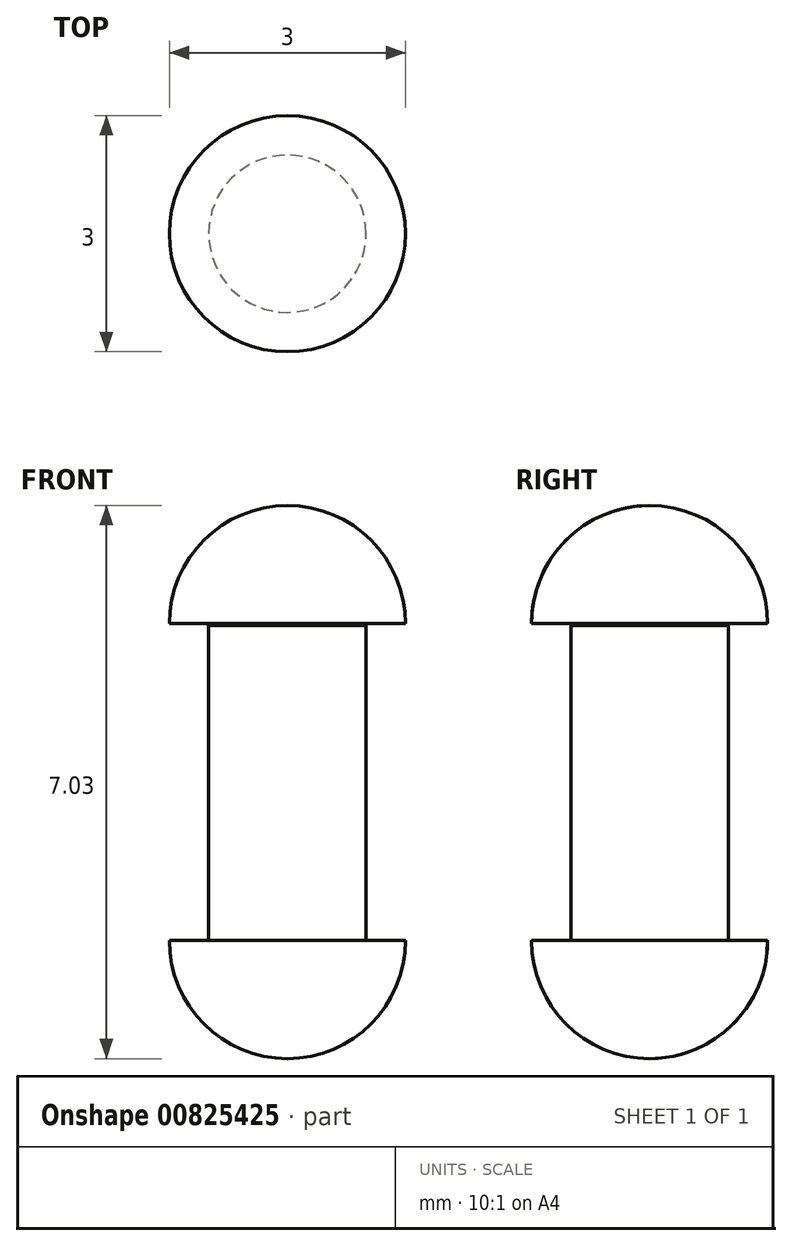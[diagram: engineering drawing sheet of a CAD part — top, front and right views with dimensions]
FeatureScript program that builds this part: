
annotation { "Feature Type Name" : "Feature", "Feature Type Description" : "" }
export const myFeature = defineFeature(function(context is Context, id is Id, definition is map)
    precondition{}
    {
        {
            var Q0;
            Q0=qCreatedBy(makeId("Top.planeOp"),FACE);
            var sketch = newSketch(context, id + "F0", { "sketchPlane" : qUnion([Q0])});
            skCircle(sketch, "E0", {"center": v(0, 0) * mm, "radius": 1 * mm});
            skSolve(sketch);
        }
        {
            var Q0;
            Q0=makeQuery(id+"F0.imprint","IMPRINT",FACE,{"disambiguationData":[TD([[makeQuery(id+"F0.imprint","IMPRINT",EDGE,{"derivedFrom":sQuery(id+"F0.wireOp",EDGE,"E0")}),1.0]])]});
            var Q1;
            Q1=sQuery(id+"F0.wireOp",EDGE,"E0");
            extrude(context, id + "F1", {"entities" : qUnion([Q0]), "surfaceEntities" : qUnion([Q1]), "depth" : 4 * mm, "offsetDistance" : 25 * mm});
        }
        {
            var Q0;
            Q0=qCreatedBy(makeId("Right.planeOp"),FACE);
            var sketch = newSketch(context, id + "F2", { "sketchPlane" : qUnion([Q0])});
            skArc(sketch, "E1", {"start": v(0, -1.5) * mm, "mid": v(1.06, -1.06) * mm, "end": v(1.5, 0) * mm});
            skLineSegment(sketch, "E2", {"start": v(0, 0) * mm, "end": v(1.5, 0) * mm});
            skLineSegment(sketch, "E3", {"start": v(0, 0) * mm, "end": v(0, -1.5) * mm});
            skSolve(sketch);
        }
        {
            var Q0;
            Q0=makeQuery(id+"F2.imprint","IMPRINT",FACE,{"disambiguationData":[TD([[makeQuery(id+"F2.imprint","IMPRINT",EDGE,{"derivedFrom":sQuery(id+"F2.wireOp",EDGE,"E1")}),1.0]])]});
            var Q1;
            Q1=sQuery(id+"F2.wireOp",EDGE,"E3");
            revolve(context, id + "F3", {"operationType" : NewBodyOperationType.ADD, "surfaceOperationType" : NewSurfaceOperationType.NEW, "entities" : qUnion([Q0]), "axis" : qUnion([Q1]), "revolveType" : RevolveType.FULL});
        }
        {
            var Q0;
            Q0=qCreatedBy(makeId("Right.planeOp"),FACE);
            var sketch = newSketch(context, id + "F4", { "sketchPlane" : qUnion([Q0])});
            skLineSegment(sketch, "E4", {"start": v(0, 4.03) * mm, "end": v(0, 0) * mm, "construction": true});
            skLineSegment(sketch, "E5", {"start": v(0, 0) * mm, "end": v(0, -1.46) * mm, "construction": true});
            skArc(sketch, "E6", {"start": v(0, 5.53) * mm, "mid": v(-1.06, 5.09) * mm, "end": v(-1.5, 4.03) * mm});
            skLineSegment(sketch, "E7", {"start": v(0, 4.03) * mm, "end": v(-1.5, 4.03) * mm});
            skLineSegment(sketch, "E8", {"start": v(0, 4.03) * mm, "end": v(0, 5.53) * mm});
            skSolve(sketch);
        }
        {
            var Q0;
            Q0=makeQuery(id+"F4.imprint","IMPRINT",FACE,{"disambiguationData":[TD([[makeQuery(id+"F4.imprint","IMPRINT",EDGE,{"derivedFrom":sQuery(id+"F4.wireOp",EDGE,"E6")}),1.0]])]});
            var Q1;
            Q1=sQuery(id+"F4.wireOp",EDGE,"E8");
            revolve(context, id + "F5", {"surfaceOperationType" : NewSurfaceOperationType.NEW, "entities" : qUnion([Q0]), "axis" : qUnion([Q1]), "revolveType" : RevolveType.FULL});
        }
    });
